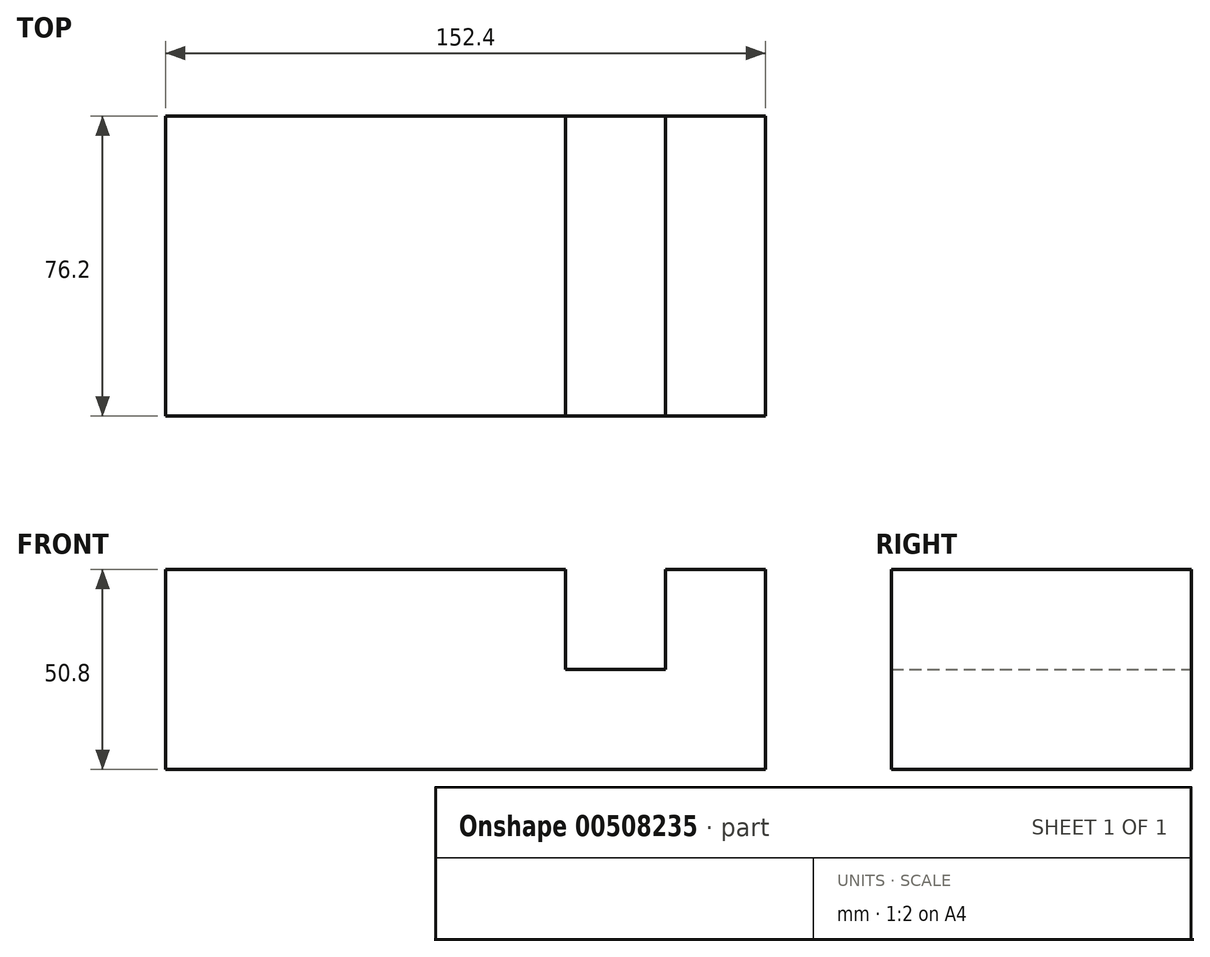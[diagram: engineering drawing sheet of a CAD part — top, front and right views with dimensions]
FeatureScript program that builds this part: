
annotation { "Feature Type Name" : "Feature", "Feature Type Description" : "" }
export const myFeature = defineFeature(function(context is Context, id is Id, definition is map)
    precondition{}
    {
        {
            var Q0;
            Q0=qCreatedBy(makeId("Front.planeOp"),FACE);
            var sketch = newSketch(context, id + "F0", { "sketchPlane" : qUnion([Q0])});
            skLineSegment(sketch, "E0", {"start": v(-32.2, 53.66) * mm, "end": v(69.4, 53.66) * mm});
            skLineSegment(sketch, "E1", {"start": v(69.4, 53.66) * mm, "end": v(69.4, 28.26) * mm});
            skLineSegment(sketch, "E2", {"start": v(69.4, 28.26) * mm, "end": v(94.8, 28.26) * mm});
            skLineSegment(sketch, "E3", {"start": v(94.8, 28.26) * mm, "end": v(94.8, 53.66) * mm});
            skLineSegment(sketch, "E4", {"start": v(94.8, 53.66) * mm, "end": v(120.2, 53.66) * mm});
            skLineSegment(sketch, "E5", {"start": v(120.2, 53.66) * mm, "end": v(120.2, 2.86) * mm});
            skLineSegment(sketch, "E6", {"start": v(120.2, 2.86) * mm, "end": v(-32.2, 2.86) * mm});
            skLineSegment(sketch, "E7", {"start": v(-32.2, 2.86) * mm, "end": v(-32.2, 53.66) * mm});
            skSolve(sketch);
        }
        {
            var Q0;
            Q0 = qSketchRegion(id + "F0", true);
            extrude(context, id + "F1", {"entities" : qUnion([Q0]), "depth" : 76.2 * mm});
        }
    });
